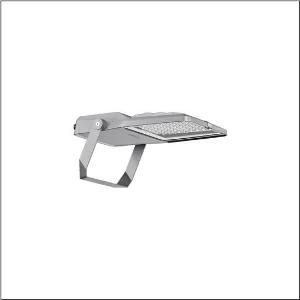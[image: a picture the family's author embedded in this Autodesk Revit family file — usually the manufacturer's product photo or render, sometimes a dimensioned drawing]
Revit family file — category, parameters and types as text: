
# Revit family: floodlight_fl_21_iq_mini___pl43_5xa7772b2a1a_654d
name_source: partatom
category: Lighting Fixtures
units: mm (PartAtom-declared; Revit-internal decimal feet)

## family parameters
Cut with Voids When Loaded = No
Host = Face
Light Source = No
Part Type = Normal
Room Calculation Point = No
Round Connector Dimension = Use Diameter
Shared = No

## types (1)
- --- (1 x LED, 6400 lm, 45.5 W, 3000K)
    Apparent Load = 46 VA
    CIE Flux Codes = 27 78 99 100 100
    Color Rendering = 70
    Color Temperature = 3000K
    Default Elevation = 1800 mm
    Description = Floodlight FL 21 iQ mini, floodlight, primary light control with lens, of PMMA, primary optical cover: protective disc, of toughened safety glass, transparent, light distribution: PL43, light emission: direct distribution, installation type: surface-mounted, lamps: LED, High Power LED, rated values: 6.400lm | 45,5W | 140,7lm/W (begin service life); end service life: 6.400lm | 48W; at 50% lumin. flux: 3.200lm | 21,5W | 148,8lm/W, colour temperature: 3000K, colour rendering: CRI > 70, light colour: 730, light setting 1 begin service life: 100% | 6.400lm | 45,5W | 140,7lm/W | 3.000K, light setting 1 end service life: 48W, further light settings possible, control: Street-Remote, Auto-Match, Temp-Guard, Night-Set, Smart-Wire, Desk-Remote (wireless, voltage-free reading and setting of iQ features in the workshop via application-optimized NFC function/RFID function), optimised constant luminous flux control (CLO 2.0), pre-setting: linear dimming characteristic, with terminal, 6-pole, mains connection: 220..240V, AC, 50/60Hz, luminaire housing, of diecast aluminium, powder-coated, SITECO metallic grey (DB 702S), corrosivity category C5 mid according to DIN EN ISO 12944suitable for swimming poolschlorine-resistant, sealing non-destructively replaceable, mounting bracket, of steel, galvanised, powder-coated, SITECO metallic grey (DB 702S), protection rating (complete): IP66, insulation class (complete): insulation class II (safety insulation), certification: CE, ENEC, VDE, protection symbol: D, impact resistance: IK08, permissible operating ambient temperature: -40..+40°C, permissible operating ambient temperature for outdoor applications: -40..+50°C, standard: DIN EN 12944, LABS conformity tested according to VDMA 24364:2018-05, packaging unit: 1 piece

Light Distribution: PL43
    Height = 70 mm
    Lamp = 1 x LED
    Lamp Light Flux = 6400 lm
    Lamp Power = 45.5 W
    Lamp count = 1
    Length = 485 mm
    Luminous efficacy = 141 lm/W
    Manufacturer = Siteco
    ModVariant = No
    Model = 5XA7772B2A1A
    Mounting Place = Pole
    Mounting Type = Pole annexe
    Number of Poles = 1
    OnlyDefault = Yes
    Power Factor = 1
    Product Name = Floodlight FL 21 iQ mini | PL43
    Product group = floodlight | pylon annexe
    ProductGroupID = 6201
    Protection Class = Protection class II
    Protection Degree = IP 66
    RLX_Detail_Level = 1
    RLX_Emergency_Light_Flux = 0 lm
    RLX_Emergency_Type = 0
    RLX_Emergency_Type_DB = No
    RlxData = <blob elided: 96313 chars, md5=edb62715>
    Socket = socket
    Standby Power = 0 W
    System Light Flux = 6400 lm
    System Power = 46 W
    Type Comments = factory setting: luminous flux: 100 % | dim-lin: 254 | 463 mA
    Type Image = l_1006845.jpg
    URL = http://relux.com
    VarID = @adj_163987
    Voltage = 0 V
    Weight = 0.00 kg
    Width = 337 mm

## geometry (parser evidence)
native form markers: Blend x4, Sweep x14
no freeform markers — native parametric forms only
